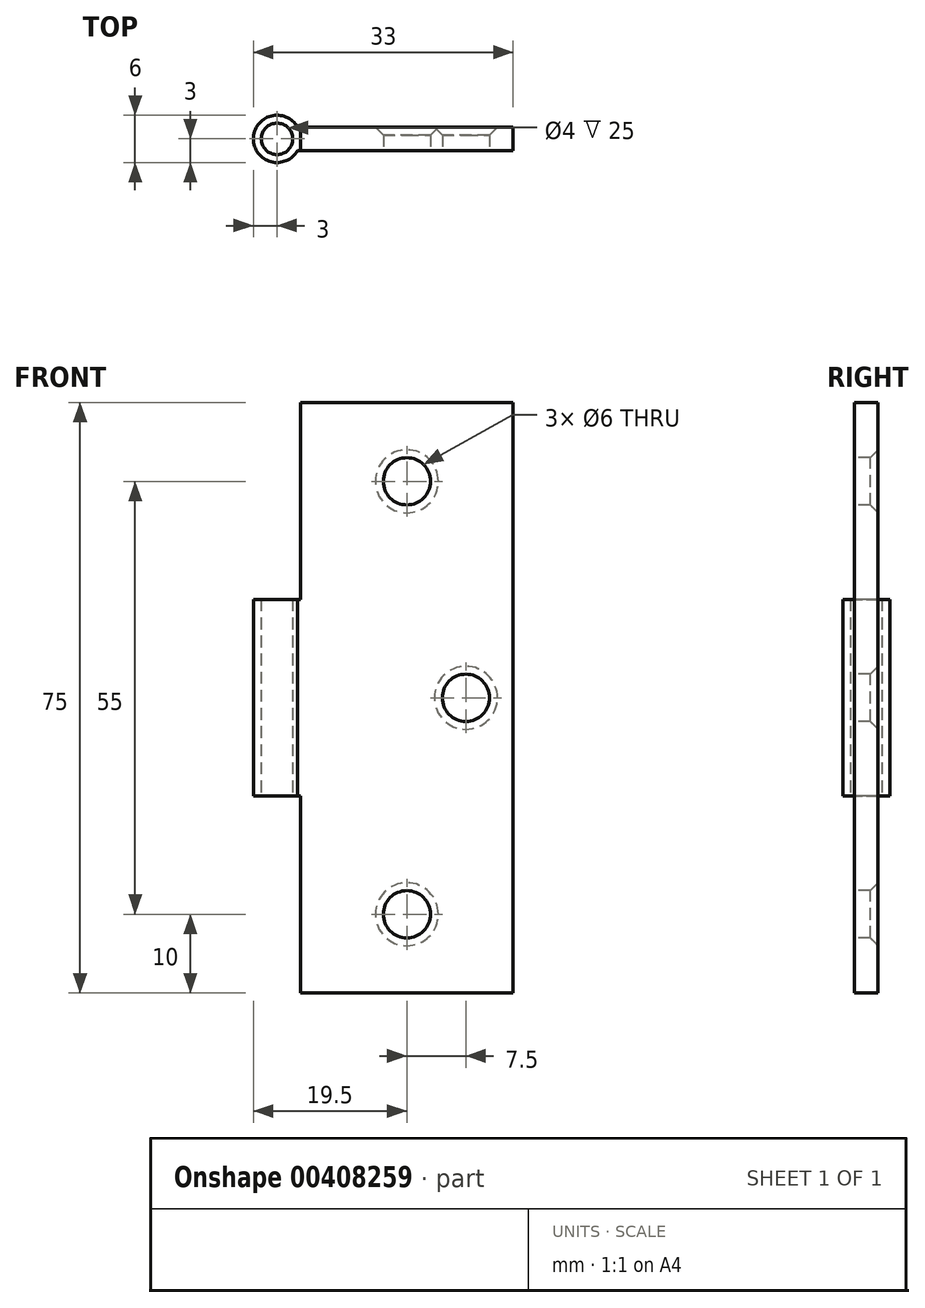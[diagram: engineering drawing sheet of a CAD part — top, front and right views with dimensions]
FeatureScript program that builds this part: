
annotation { "Feature Type Name" : "Feature", "Feature Type Description" : "" }
export const myFeature = defineFeature(function(context is Context, id is Id, definition is map)
    precondition{}
    {
        {
            var Q0;
            Q0=qCreatedBy(makeId("Top.planeOp"),FACE);
            var sketch = newSketch(context, id + "F0", { "sketchPlane" : qUnion([Q0])});
            skArc(sketch, "E0", {"start": v(2.6, 1.5) * mm, "mid": v(-3, 0) * mm, "end": v(2.6, -1.5) * mm});
            skCircle(sketch, "E1", {"center": v(0, 0) * mm, "radius": 2 * mm});
            skLineSegment(sketch, "E2.MirrorCS", {"start": v(2.6, 1.5) * mm, "end": v(30, 1.5) * mm});
            skLineSegment(sketch, "E3", {"start": v(30, 1.5) * mm, "end": v(30, -1.5) * mm});
            skPoint(sketch, "E4.orphan", {"position": v(0, 1.5) * mm});
            skLineSegment(sketch, "E5.trimOffspring", {"start": v(2.6, -1.5) * mm, "end": v(30, -1.5) * mm});
            skPoint(sketch, "E6.0.start.orphan", {"position": v(0, -1.5) * mm});
            skSolve(sketch);
        }
        {
            var Q0;
            Q0 = qSketchRegion(id + "F0", true);
            extrude(context, id + "F1", {"entities" : qUnion([Q0]), "depth" : 75 * mm});
        }
        {
            var Q0;
            Q0=qCreatedBy(makeId("Front.planeOp"),FACE);
            var sketch = newSketch(context, id + "F2", { "sketchPlane" : qUnion([Q0])});
            skLineSegment(sketch, "E7", {"start": v(0, 0) * mm, "end": v(0, 25) * mm});
            skLineSegment(sketch, "E8", {"start": v(0, 0) * mm, "end": v(0, 50) * mm});
            skLineSegment(sketch, "E9", {"start": v(0, 50) * mm, "end": v(0, 75) * mm});
            skLineSegment(sketch, "E10.bottom", {"start": v(3, 75) * mm, "end": v(-3, 75) * mm});
            skLineSegment(sketch, "E10.top", {"start": v(3, 50) * mm, "end": v(-3, 50) * mm});
            skLineSegment(sketch, "E10.left", {"start": v(3, 75) * mm, "end": v(3, 50) * mm});
            skLineSegment(sketch, "E10.right", {"start": v(-3, 75) * mm, "end": v(-3, 50) * mm});
            skPoint(sketch, "E10.middle", {"position": v(0, 62.5) * mm});
            skLineSegment(sketch, "E11.bottom", {"start": v(3, 25) * mm, "end": v(-3, 25) * mm});
            skLineSegment(sketch, "E11.top", {"start": v(3, 0) * mm, "end": v(-3, 0) * mm});
            skLineSegment(sketch, "E11.left", {"start": v(3, 25) * mm, "end": v(3, 0) * mm});
            skLineSegment(sketch, "E11.right", {"start": v(-3, 25) * mm, "end": v(-3, 0) * mm});
            skPoint(sketch, "E11.middle", {"position": v(0, 12.5) * mm});
            skSolve(sketch);
        }
        {
            var Q0;
            Q0 = qSketchRegion(id + "F2", true);
            extrude(context, id + "F3", {"entities" : qUnion([Q0]), "operationType" : NewBodyOperationType.REMOVE, "oppositeDirection" : true, "depth" : 25 * mm, "symmetric" : true});
        }
        {
            var Q0;
            Q0=makeQuery(id+"F1.opExtrude","SWEPT_FACE",FACE,{"disambiguationData":[OSD([sQuery(id+"F0.wireOp",EDGE,"E2.MirrorCS")])]});
            var sketch = newSketch(context, id + "F4", { "sketchPlane" : qUnion([Q0])});
            skLineSegment(sketch, "E12", {"start": v(-16.5, 0) * mm, "end": v(-16.5, 75) * mm});
            skLineSegment(sketch, "E13", {"start": v(-30, 37.5) * mm, "end": v(-3, 37.5) * mm});
            skLineSegment(sketch, "E14.0", {"start": v(-3, 10) * mm, "end": v(-30, 10) * mm});
            skLineSegment(sketch, "E15.5", {"start": v(-8, 30) * mm, "end": v(-7.6, 30) * mm});
            skLineSegment(sketch, "E15.7", {"start": v(-7.6, 45) * mm, "end": v(-8, 45) * mm});
            skLineSegment(sketch, "E16.0", {"start": v(-3, 65) * mm, "end": v(-30, 65) * mm});
            skLineSegment(sketch, "E17.0", {"start": v(-24, 0) * mm, "end": v(-24, 75) * mm});
            skPoint(sketch, "E18", {"position": v(-16.5, 65) * mm});
            skPoint(sketch, "E19", {"position": v(-24, 37.5) * mm});
            skPoint(sketch, "E20", {"position": v(-16.5, 10) * mm});
            skSolve(sketch);
        }
        {
            var Q0;
            Q0=sQuery(id+"F4.wireOp",VERTEX,"E18");
            var Q1;
            Q1=sQuery(id+"F4.wireOp",VERTEX,"E19");
            var Q2;
            Q2=sQuery(id+"F4.wireOp",VERTEX,"E20");
            var Q3;
            Q3=makeQuery(id+"F1.opExtrude","SWEPT_BODY",BODY,{"disambiguationData":[OSD([sQuery(id+"F0.wireOp",EDGE,"E0"),sQuery(id+"F0.wireOp",EDGE,"E1"),sQuery(id+"F0.wireOp",EDGE,"E2.MirrorCS"),sQuery(id+"F0.wireOp",EDGE,"E3"),sQuery(id+"F0.wireOp",EDGE,"E5.trimOffspring")])]});
            hole(context, id + "F5", {"style" : HoleStyle.C_SINK, "endStyle" : HoleEndStyle.THROUGH, "holeDiameter" : 6 * mm, "cSinkDiameter" : 8 * mm, "cSinkAngle" : 90 * degree, "isTappedThrough" : true, "tappedDepth" : 12 * mm, "tapClearance" : 3, "locations" : qUnion([Q0, Q1, Q2]), "scope" : qUnion([Q3])});
        }
    });
